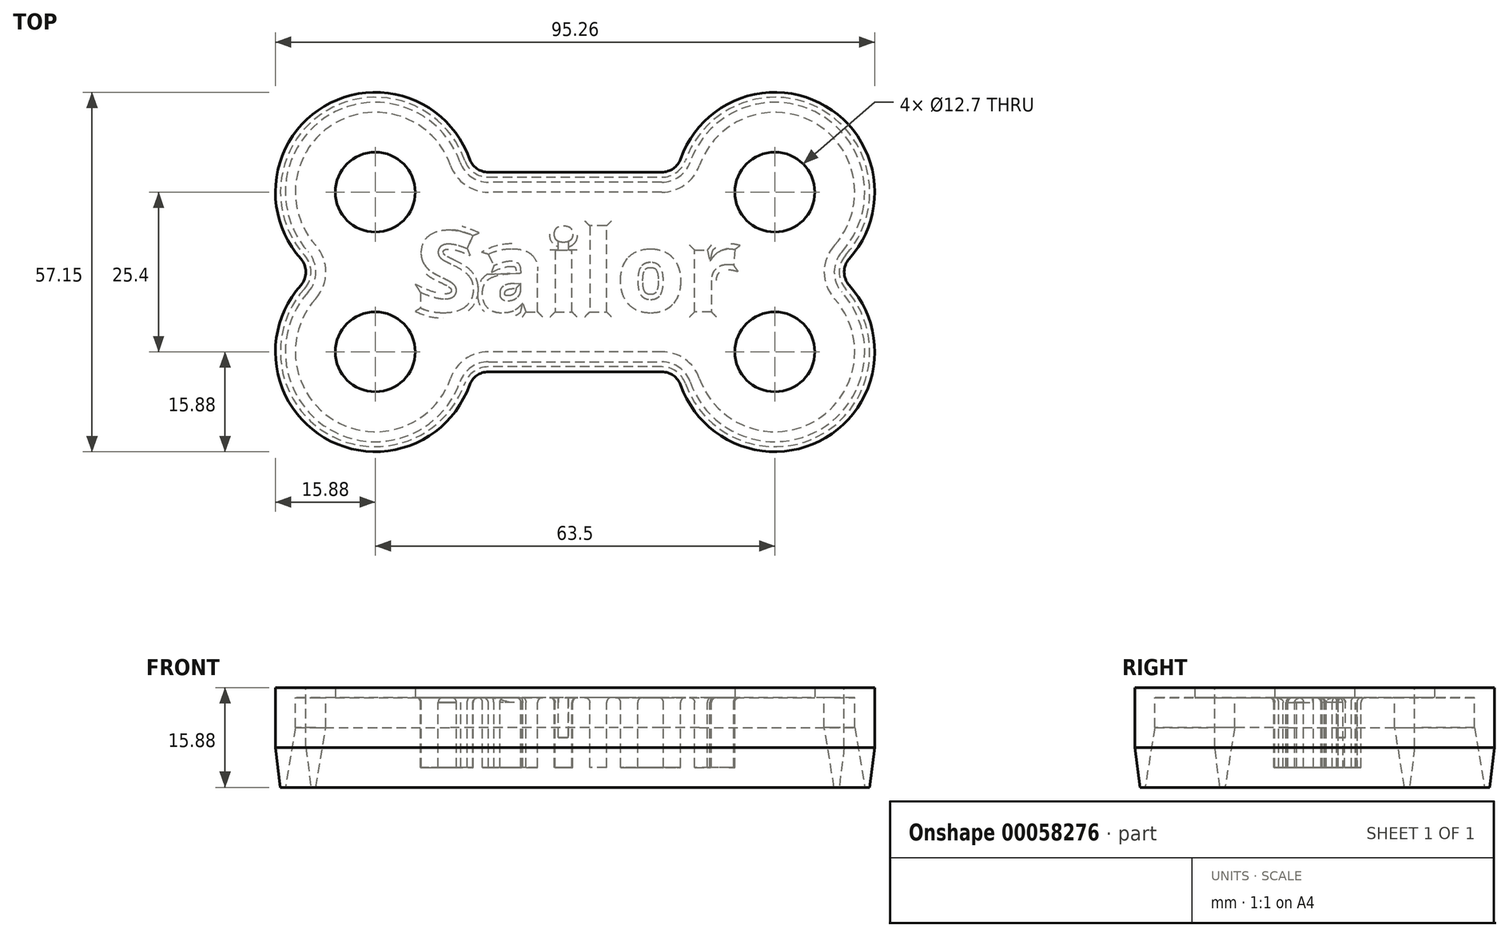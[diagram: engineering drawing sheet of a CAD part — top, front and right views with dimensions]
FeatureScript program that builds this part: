
annotation { "Feature Type Name" : "Feature", "Feature Type Description" : "" }
export const myFeature = defineFeature(function(context is Context, id is Id, definition is map)
    precondition{}
    {
        {
            var Q0;
            Q0=qCreatedBy(makeId("Top.planeOp"),FACE);
            var sketch = newSketch(context, id + "F0", { "sketchPlane" : qUnion([Q0])});
            skText(sketch, "E0", { "text": "Sailor", "fontName": "OpenSans-Bold.ttf"});
            const initialGuessF0  = {"E0": [0, 0, 1, 0, 0.01298]};
            skSetInitialGuess(sketch, initialGuessF0);
            skSolve(sketch);
        }
        {
            var Q0;
            Q0 = qSketchRegion(id + "F0", true);
            extrude(context, id + "F1", {"entities" : qUnion([Q0]), "oppositeDirection" : true, "depth" : 12.7 * mm});
        }
        {
            var Q0;
            Q0=qCreatedBy(makeId("Top.planeOp"),FACE);
            var sketch = newSketch(context, id + "F2", { "sketchPlane" : qUnion([Q0])});
            skLineSegment(sketch, "E1.bottom", {"start": v(11.61, 19.05) * mm, "end": v(39.19, 19.05) * mm});
            skLineSegment(sketch, "E1.top", {"start": v(11.61, -6.35) * mm, "end": v(39.19, -6.35) * mm});
            skArc(sketch, "E2", {"start": v(5.62, 23.28) * mm, "mid": v(-12.82, 29.98) * mm, "end": v(-15.82, 10.58) * mm});
            skArc(sketch, "E3", {"start": v(-15.82, 2.12) * mm, "mid": v(-12.82, -17.28) * mm, "end": v(5.62, -10.58) * mm});
            skArc(sketch, "E4", {"start": v(66.62, 10.58) * mm, "mid": v(63.62, 29.98) * mm, "end": v(45.18, 23.28) * mm});
            skArc(sketch, "E5", {"start": v(45.18, -10.58) * mm, "mid": v(63.62, -17.28) * mm, "end": v(66.62, 2.12) * mm});
            skPoint(sketch, "E6.visualSharp", {"position": v(-6.35, 6.35) * mm});
            skArc(sketch, "E6.filletArc", {"start": v(-15.82, 2.12) * mm, "mid": v(-14.2, 6.35) * mm, "end": v(-15.82, 10.58) * mm});
            skPoint(sketch, "E7.visualSharp", {"position": v(57.15, 6.35) * mm});
            skArc(sketch, "E7.filletArc", {"start": v(66.62, 10.58) * mm, "mid": v(65, 6.35) * mm, "end": v(66.62, 2.12) * mm});
            skPoint(sketch, "E8.visualSharp", {"position": v(44.45, 19.05) * mm});
            skArc(sketch, "E8.filletArc", {"start": v(39.19, 19.05) * mm, "mid": v(42.86, 20.22) * mm, "end": v(45.18, 23.28) * mm});
            skPoint(sketch, "E9.visualSharp", {"position": v(6.35, 19.05) * mm});
            skArc(sketch, "E9.filletArc", {"start": v(5.62, 23.28) * mm, "mid": v(7.94, 20.22) * mm, "end": v(11.61, 19.05) * mm});
            skPoint(sketch, "E10.visualSharp", {"position": v(6.35, -6.35) * mm});
            skArc(sketch, "E10.filletArc", {"start": v(11.61, -6.35) * mm, "mid": v(7.94, -7.52) * mm, "end": v(5.62, -10.58) * mm});
            skPoint(sketch, "E11.visualSharp", {"position": v(44.45, -6.35) * mm});
            skArc(sketch, "E11.filletArc", {"start": v(45.18, -10.58) * mm, "mid": v(42.86, -7.52) * mm, "end": v(39.19, -6.35) * mm});
            skArc(sketch, "E12.0", {"start": v(8.62, 24.34) * mm, "mid": v(9.78, 22.8) * mm, "end": v(11.61, 22.23) * mm});
            skArc(sketch, "E12.1", {"start": v(42.18, -11.64) * mm, "mid": v(65.24, -20) * mm, "end": v(68.98, 4.23) * mm});
            skArc(sketch, "E12.2", {"start": v(68.98, 8.47) * mm, "mid": v(68.17, 6.35) * mm, "end": v(68.98, 4.23) * mm});
            skArc(sketch, "E12.3", {"start": v(68.98, 8.47) * mm, "mid": v(65.24, 32.7) * mm, "end": v(42.18, 24.34) * mm});
            skArc(sketch, "E12.4", {"start": v(39.19, 22.23) * mm, "mid": v(41.02, 22.8) * mm, "end": v(42.18, 24.34) * mm});
            skArc(sketch, "E12.5", {"start": v(42.18, -11.64) * mm, "mid": v(41.02, -10.1) * mm, "end": v(39.19, -9.52) * mm});
            skLineSegment(sketch, "E12.6", {"start": v(11.61, 22.22) * mm, "end": v(39.19, 22.23) * mm});
            skLineSegment(sketch, "E12.7", {"start": v(11.61, -9.53) * mm, "end": v(39.19, -9.52) * mm});
            skArc(sketch, "E12.8", {"start": v(11.61, -9.53) * mm, "mid": v(9.78, -10.1) * mm, "end": v(8.62, -11.64) * mm});
            skArc(sketch, "E12.9", {"start": v(-18.18, 4.23) * mm, "mid": v(-14.44, -20) * mm, "end": v(8.62, -11.64) * mm});
            skArc(sketch, "E12.10", {"start": v(-18.18, 4.23) * mm, "mid": v(-17.37, 6.35) * mm, "end": v(-18.18, 8.47) * mm});
            skArc(sketch, "E12.11", {"start": v(8.62, 24.34) * mm, "mid": v(-14.44, 32.7) * mm, "end": v(-18.18, 8.47) * mm});
            skSolve(sketch);
        }
        {
            var Q0;
            Q0 = qSketchRegion(id + "F2", true);
            extrude(context, id + "F3", {"entities" : qUnion([Q0]), "oppositeDirection" : true, "depth" : 15.88 * mm});
        }
        {
            var Q0;
            Q0=qCreatedBy(makeId("Top.planeOp"),FACE);
            var sketch = newSketch(context, id + "F4", { "sketchPlane" : qUnion([Q0])});
            skArc(sketch, "E13.0", {"start": v(-18.18, 8.47) * mm, "mid": v(-14.44, 32.7) * mm, "end": v(8.62, 24.34) * mm});
            skArc(sketch, "E14.0", {"start": v(8.62, 24.34) * mm, "mid": v(9.78, 22.8) * mm, "end": v(11.61, 22.23) * mm});
            skLineSegment(sketch, "E15.0", {"start": v(11.61, 22.22) * mm, "end": v(39.19, 22.23) * mm});
            skArc(sketch, "E16.0", {"start": v(39.19, 22.23) * mm, "mid": v(41.02, 22.8) * mm, "end": v(42.18, 24.34) * mm});
            skArc(sketch, "E17.0", {"start": v(42.18, 24.34) * mm, "mid": v(65.24, 32.7) * mm, "end": v(68.98, 8.47) * mm});
            skArc(sketch, "E18.0", {"start": v(68.98, 8.47) * mm, "mid": v(68.17, 6.35) * mm, "end": v(68.98, 4.23) * mm});
            skArc(sketch, "E19.0", {"start": v(68.98, 4.23) * mm, "mid": v(65.24, -20) * mm, "end": v(42.18, -11.64) * mm});
            skArc(sketch, "E20.0", {"start": v(42.18, -11.64) * mm, "mid": v(41.02, -10.1) * mm, "end": v(39.19, -9.52) * mm});
            skLineSegment(sketch, "E21.0", {"start": v(39.19, -9.52) * mm, "end": v(11.61, -9.53) * mm});
            skArc(sketch, "E22.0", {"start": v(11.61, -9.53) * mm, "mid": v(9.78, -10.1) * mm, "end": v(8.62, -11.64) * mm});
            skArc(sketch, "E23.0", {"start": v(8.62, -11.64) * mm, "mid": v(-14.44, -20) * mm, "end": v(-18.18, 4.23) * mm});
            skArc(sketch, "E24.0", {"start": v(-18.18, 4.23) * mm, "mid": v(-17.37, 6.35) * mm, "end": v(-18.18, 8.47) * mm});
            skSolve(sketch);
        }
        {
            var Q0;
            Q0 = qSketchRegion(id + "F4", true);
            extrude(context, id + "F5", {"entities" : qUnion([Q0]), "operationType" : NewBodyOperationType.ADD, "oppositeDirection" : true, "depth" : 1.59 * mm});
        }
        {
            var Q0;
            Q0=makeQuery(id+"F5.boolean.opBoolean","SPLIT",FACE,{"disambiguationData":[TD([makeQuery(id+"F1.opExtrude","SWEPT_FACE",FACE,{"disambiguationData":[OSD([sQuery(id+"F0.wireOp",EDGE,"E0.sketch_text.stroke-0")])]})])],"derivedFrom":makeQuery(id+"F5.opExtrude","CAP_FACE",FACE,{"disambiguationData":[OSD([sQuery(id+"F4.wireOp",EDGE,"E13.0"),sQuery(id+"F4.wireOp",EDGE,"E14.0"),sQuery(id+"F4.wireOp",EDGE,"E15.0"),sQuery(id+"F4.wireOp",EDGE,"E16.0"),sQuery(id+"F4.wireOp",EDGE,"E17.0"),sQuery(id+"F4.wireOp",EDGE,"E18.0"),sQuery(id+"F4.wireOp",EDGE,"E19.0"),sQuery(id+"F4.wireOp",EDGE,"E20.0"),sQuery(id+"F4.wireOp",EDGE,"E21.0"),sQuery(id+"F4.wireOp",EDGE,"E22.0"),sQuery(id+"F4.wireOp",EDGE,"E23.0"),sQuery(id+"F4.wireOp",EDGE,"E24.0")])],"isStart":false})});
            var sketch = newSketch(context, id + "F6", { "sketchPlane" : qUnion([Q0])});
            skLineSegment(sketch, "E25", {"start": v(22.73, -8.79) * mm, "end": v(22.73, -11.84) * mm});
            skLineSegment(sketch, "E26", {"start": v(22.73, -11.84) * mm, "end": v(24.32, -11.84) * mm});
            skLineSegment(sketch, "E27", {"start": v(24.32, -11.84) * mm, "end": v(24.32, -8.79) * mm});
            skLineSegment(sketch, "E28", {"start": v(24.32, -8.79) * mm, "end": v(22.73, -8.79) * mm});
            skSolve(sketch);
        }
        {
            var Q0;
            Q0 = qSketchRegion(id + "F6", true);
            extrude(context, id + "F7", {"entities" : qUnion([Q0]), "operationType" : NewBodyOperationType.ADD, "depth" : 6.35 * mm});
        }
        {
            var Q0;
            Q0=makeQuery(id+"F5.boolean.opBoolean","INTERSECT",EDGE,{"derivedFrom":[makeQuery(id+"F1.opExtrude","SWEPT_FACE",FACE,{"disambiguationData":[OSD([sQuery(id+"F0.wireOp",EDGE,"E0.sketch_text.stroke-14")])]}),makeQuery(id+"F5.opExtrude","CAP_FACE",FACE,{"disambiguationData":[OSD([sQuery(id+"F4.wireOp",EDGE,"E13.0"),sQuery(id+"F4.wireOp",EDGE,"E14.0"),sQuery(id+"F4.wireOp",EDGE,"E15.0"),sQuery(id+"F4.wireOp",EDGE,"E16.0"),sQuery(id+"F4.wireOp",EDGE,"E17.0"),sQuery(id+"F4.wireOp",EDGE,"E18.0"),sQuery(id+"F4.wireOp",EDGE,"E19.0"),sQuery(id+"F4.wireOp",EDGE,"E20.0"),sQuery(id+"F4.wireOp",EDGE,"E21.0"),sQuery(id+"F4.wireOp",EDGE,"E22.0"),sQuery(id+"F4.wireOp",EDGE,"E23.0"),sQuery(id+"F4.wireOp",EDGE,"E24.0")])],"isStart":false})]});
            var Q1;
            Q1=makeQuery(id+"F5.boolean.opBoolean","INTERSECT",EDGE,{"derivedFrom":[makeQuery(id+"F1.opExtrude","SWEPT_FACE",FACE,{"disambiguationData":[OSD([sQuery(id+"F0.wireOp",EDGE,"E0.sketch_text.stroke-7")])]}),makeQuery(id+"F5.opExtrude","CAP_FACE",FACE,{"disambiguationData":[OSD([sQuery(id+"F4.wireOp",EDGE,"E13.0"),sQuery(id+"F4.wireOp",EDGE,"E14.0"),sQuery(id+"F4.wireOp",EDGE,"E15.0"),sQuery(id+"F4.wireOp",EDGE,"E16.0"),sQuery(id+"F4.wireOp",EDGE,"E17.0"),sQuery(id+"F4.wireOp",EDGE,"E18.0"),sQuery(id+"F4.wireOp",EDGE,"E19.0"),sQuery(id+"F4.wireOp",EDGE,"E20.0"),sQuery(id+"F4.wireOp",EDGE,"E21.0"),sQuery(id+"F4.wireOp",EDGE,"E22.0"),sQuery(id+"F4.wireOp",EDGE,"E23.0"),sQuery(id+"F4.wireOp",EDGE,"E24.0")])],"isStart":false})]});
            var Q2;
            Q2=makeQuery(id+"F5.boolean.opBoolean","INTERSECT",EDGE,{"derivedFrom":[makeQuery(id+"F1.opExtrude","SWEPT_FACE",FACE,{"disambiguationData":[OSD([sQuery(id+"F0.wireOp",EDGE,"E0.sketch_text.stroke-3")])]}),makeQuery(id+"F5.opExtrude","CAP_FACE",FACE,{"disambiguationData":[OSD([sQuery(id+"F4.wireOp",EDGE,"E13.0"),sQuery(id+"F4.wireOp",EDGE,"E14.0"),sQuery(id+"F4.wireOp",EDGE,"E15.0"),sQuery(id+"F4.wireOp",EDGE,"E16.0"),sQuery(id+"F4.wireOp",EDGE,"E17.0"),sQuery(id+"F4.wireOp",EDGE,"E18.0"),sQuery(id+"F4.wireOp",EDGE,"E19.0"),sQuery(id+"F4.wireOp",EDGE,"E20.0"),sQuery(id+"F4.wireOp",EDGE,"E21.0"),sQuery(id+"F4.wireOp",EDGE,"E22.0"),sQuery(id+"F4.wireOp",EDGE,"E23.0"),sQuery(id+"F4.wireOp",EDGE,"E24.0")])],"isStart":false})]});
            var Q3;
            Q3=makeQuery(id+"F5.boolean.opBoolean","INTERSECT",EDGE,{"derivedFrom":[makeQuery(id+"F1.opExtrude","SWEPT_FACE",FACE,{"disambiguationData":[OSD([sQuery(id+"F0.wireOp",EDGE,"E0.sketch_text.stroke-1")])]}),makeQuery(id+"F5.opExtrude","CAP_FACE",FACE,{"disambiguationData":[OSD([sQuery(id+"F4.wireOp",EDGE,"E13.0"),sQuery(id+"F4.wireOp",EDGE,"E14.0"),sQuery(id+"F4.wireOp",EDGE,"E15.0"),sQuery(id+"F4.wireOp",EDGE,"E16.0"),sQuery(id+"F4.wireOp",EDGE,"E17.0"),sQuery(id+"F4.wireOp",EDGE,"E18.0"),sQuery(id+"F4.wireOp",EDGE,"E19.0"),sQuery(id+"F4.wireOp",EDGE,"E20.0"),sQuery(id+"F4.wireOp",EDGE,"E21.0"),sQuery(id+"F4.wireOp",EDGE,"E22.0"),sQuery(id+"F4.wireOp",EDGE,"E23.0"),sQuery(id+"F4.wireOp",EDGE,"E24.0")])],"isStart":false})]});
            var Q4;
            Q4=makeQuery(id+"F5.boolean.opBoolean","INTERSECT",EDGE,{"derivedFrom":[makeQuery(id+"F1.opExtrude","SWEPT_FACE",FACE,{"disambiguationData":[OSD([sQuery(id+"F0.wireOp",EDGE,"E0.sketch_text.stroke-20")])]}),makeQuery(id+"F5.opExtrude","CAP_FACE",FACE,{"disambiguationData":[OSD([sQuery(id+"F4.wireOp",EDGE,"E13.0"),sQuery(id+"F4.wireOp",EDGE,"E14.0"),sQuery(id+"F4.wireOp",EDGE,"E15.0"),sQuery(id+"F4.wireOp",EDGE,"E16.0"),sQuery(id+"F4.wireOp",EDGE,"E17.0"),sQuery(id+"F4.wireOp",EDGE,"E18.0"),sQuery(id+"F4.wireOp",EDGE,"E19.0"),sQuery(id+"F4.wireOp",EDGE,"E20.0"),sQuery(id+"F4.wireOp",EDGE,"E21.0"),sQuery(id+"F4.wireOp",EDGE,"E22.0"),sQuery(id+"F4.wireOp",EDGE,"E23.0"),sQuery(id+"F4.wireOp",EDGE,"E24.0")])],"isStart":false})]});
            var Q5;
            Q5=makeQuery(id+"F5.boolean.opBoolean","INTERSECT",EDGE,{"derivedFrom":[makeQuery(id+"F1.opExtrude","SWEPT_FACE",FACE,{"disambiguationData":[OSD([sQuery(id+"F0.wireOp",EDGE,"E0.sketch_text.stroke-18")])]}),makeQuery(id+"F5.opExtrude","CAP_FACE",FACE,{"disambiguationData":[OSD([sQuery(id+"F4.wireOp",EDGE,"E13.0"),sQuery(id+"F4.wireOp",EDGE,"E14.0"),sQuery(id+"F4.wireOp",EDGE,"E15.0"),sQuery(id+"F4.wireOp",EDGE,"E16.0"),sQuery(id+"F4.wireOp",EDGE,"E17.0"),sQuery(id+"F4.wireOp",EDGE,"E18.0"),sQuery(id+"F4.wireOp",EDGE,"E19.0"),sQuery(id+"F4.wireOp",EDGE,"E20.0"),sQuery(id+"F4.wireOp",EDGE,"E21.0"),sQuery(id+"F4.wireOp",EDGE,"E22.0"),sQuery(id+"F4.wireOp",EDGE,"E23.0"),sQuery(id+"F4.wireOp",EDGE,"E24.0")])],"isStart":false})]});
            var Q6;
            Q6=makeQuery(id+"F5.boolean.opBoolean","INTERSECT",EDGE,{"derivedFrom":[makeQuery(id+"F1.opExtrude","SWEPT_FACE",FACE,{"disambiguationData":[OSD([sQuery(id+"F0.wireOp",EDGE,"E0.sketch_text.stroke-32")])]}),makeQuery(id+"F5.opExtrude","CAP_FACE",FACE,{"disambiguationData":[OSD([sQuery(id+"F4.wireOp",EDGE,"E13.0"),sQuery(id+"F4.wireOp",EDGE,"E14.0"),sQuery(id+"F4.wireOp",EDGE,"E15.0"),sQuery(id+"F4.wireOp",EDGE,"E16.0"),sQuery(id+"F4.wireOp",EDGE,"E17.0"),sQuery(id+"F4.wireOp",EDGE,"E18.0"),sQuery(id+"F4.wireOp",EDGE,"E19.0"),sQuery(id+"F4.wireOp",EDGE,"E20.0"),sQuery(id+"F4.wireOp",EDGE,"E21.0"),sQuery(id+"F4.wireOp",EDGE,"E22.0"),sQuery(id+"F4.wireOp",EDGE,"E23.0"),sQuery(id+"F4.wireOp",EDGE,"E24.0")])],"isStart":false})]});
            var Q7;
            Q7=makeQuery(id+"F5.boolean.opBoolean","INTERSECT",EDGE,{"derivedFrom":[makeQuery(id+"F1.opExtrude","SWEPT_FACE",FACE,{"disambiguationData":[OSD([sQuery(id+"F0.wireOp",EDGE,"E0.sketch_text.stroke-28")])]}),makeQuery(id+"F5.opExtrude","CAP_FACE",FACE,{"disambiguationData":[OSD([sQuery(id+"F4.wireOp",EDGE,"E13.0"),sQuery(id+"F4.wireOp",EDGE,"E14.0"),sQuery(id+"F4.wireOp",EDGE,"E15.0"),sQuery(id+"F4.wireOp",EDGE,"E16.0"),sQuery(id+"F4.wireOp",EDGE,"E17.0"),sQuery(id+"F4.wireOp",EDGE,"E18.0"),sQuery(id+"F4.wireOp",EDGE,"E19.0"),sQuery(id+"F4.wireOp",EDGE,"E20.0"),sQuery(id+"F4.wireOp",EDGE,"E21.0"),sQuery(id+"F4.wireOp",EDGE,"E22.0"),sQuery(id+"F4.wireOp",EDGE,"E23.0"),sQuery(id+"F4.wireOp",EDGE,"E24.0")])],"isStart":false})]});
            var Q8;
            Q8=makeQuery(id+"F5.boolean.opBoolean","INTERSECT",EDGE,{"derivedFrom":[makeQuery(id+"F1.opExtrude","SWEPT_FACE",FACE,{"disambiguationData":[OSD([sQuery(id+"F0.wireOp",EDGE,"E0.sketch_text.stroke-45")])]}),makeQuery(id+"F5.opExtrude","CAP_FACE",FACE,{"disambiguationData":[OSD([sQuery(id+"F4.wireOp",EDGE,"E13.0"),sQuery(id+"F4.wireOp",EDGE,"E14.0"),sQuery(id+"F4.wireOp",EDGE,"E15.0"),sQuery(id+"F4.wireOp",EDGE,"E16.0"),sQuery(id+"F4.wireOp",EDGE,"E17.0"),sQuery(id+"F4.wireOp",EDGE,"E18.0"),sQuery(id+"F4.wireOp",EDGE,"E19.0"),sQuery(id+"F4.wireOp",EDGE,"E20.0"),sQuery(id+"F4.wireOp",EDGE,"E21.0"),sQuery(id+"F4.wireOp",EDGE,"E22.0"),sQuery(id+"F4.wireOp",EDGE,"E23.0"),sQuery(id+"F4.wireOp",EDGE,"E24.0")])],"isStart":false})]});
            var Q9;
            Q9=makeQuery(id+"F5.boolean.opBoolean","INTERSECT",EDGE,{"derivedFrom":[makeQuery(id+"F1.opExtrude","SWEPT_FACE",FACE,{"disambiguationData":[OSD([sQuery(id+"F0.wireOp",EDGE,"E0.sketch_text.stroke-44")])]}),makeQuery(id+"F5.opExtrude","CAP_FACE",FACE,{"disambiguationData":[OSD([sQuery(id+"F4.wireOp",EDGE,"E13.0"),sQuery(id+"F4.wireOp",EDGE,"E14.0"),sQuery(id+"F4.wireOp",EDGE,"E15.0"),sQuery(id+"F4.wireOp",EDGE,"E16.0"),sQuery(id+"F4.wireOp",EDGE,"E17.0"),sQuery(id+"F4.wireOp",EDGE,"E18.0"),sQuery(id+"F4.wireOp",EDGE,"E19.0"),sQuery(id+"F4.wireOp",EDGE,"E20.0"),sQuery(id+"F4.wireOp",EDGE,"E21.0"),sQuery(id+"F4.wireOp",EDGE,"E22.0"),sQuery(id+"F4.wireOp",EDGE,"E23.0"),sQuery(id+"F4.wireOp",EDGE,"E24.0")])],"isStart":false})]});
            var Q10;
            Q10=makeQuery(id+"F5.boolean.opBoolean","INTERSECT",EDGE,{"derivedFrom":[makeQuery(id+"F1.opExtrude","SWEPT_FACE",FACE,{"disambiguationData":[OSD([sQuery(id+"F0.wireOp",EDGE,"E0.sketch_text.stroke-40")])]}),makeQuery(id+"F5.opExtrude","CAP_FACE",FACE,{"disambiguationData":[OSD([sQuery(id+"F4.wireOp",EDGE,"E13.0"),sQuery(id+"F4.wireOp",EDGE,"E14.0"),sQuery(id+"F4.wireOp",EDGE,"E15.0"),sQuery(id+"F4.wireOp",EDGE,"E16.0"),sQuery(id+"F4.wireOp",EDGE,"E17.0"),sQuery(id+"F4.wireOp",EDGE,"E18.0"),sQuery(id+"F4.wireOp",EDGE,"E19.0"),sQuery(id+"F4.wireOp",EDGE,"E20.0"),sQuery(id+"F4.wireOp",EDGE,"E21.0"),sQuery(id+"F4.wireOp",EDGE,"E22.0"),sQuery(id+"F4.wireOp",EDGE,"E23.0"),sQuery(id+"F4.wireOp",EDGE,"E24.0")])],"isStart":false})]});
            var Q11;
            Q11=makeQuery(id+"F5.boolean.opBoolean","INTERSECT",EDGE,{"derivedFrom":[makeQuery(id+"F1.opExtrude","SWEPT_FACE",FACE,{"disambiguationData":[OSD([sQuery(id+"F0.wireOp",EDGE,"E0.sketch_text.stroke-39")])]}),makeQuery(id+"F5.opExtrude","CAP_FACE",FACE,{"disambiguationData":[OSD([sQuery(id+"F4.wireOp",EDGE,"E13.0"),sQuery(id+"F4.wireOp",EDGE,"E14.0"),sQuery(id+"F4.wireOp",EDGE,"E15.0"),sQuery(id+"F4.wireOp",EDGE,"E16.0"),sQuery(id+"F4.wireOp",EDGE,"E17.0"),sQuery(id+"F4.wireOp",EDGE,"E18.0"),sQuery(id+"F4.wireOp",EDGE,"E19.0"),sQuery(id+"F4.wireOp",EDGE,"E20.0"),sQuery(id+"F4.wireOp",EDGE,"E21.0"),sQuery(id+"F4.wireOp",EDGE,"E22.0"),sQuery(id+"F4.wireOp",EDGE,"E23.0"),sQuery(id+"F4.wireOp",EDGE,"E24.0")])],"isStart":false})]});
            var Q12;
            Q12=makeQuery(id+"F5.boolean.opBoolean","INTERSECT",EDGE,{"derivedFrom":[makeQuery(id+"F1.opExtrude","SWEPT_FACE",FACE,{"disambiguationData":[OSD([sQuery(id+"F0.wireOp",EDGE,"E0.sketch_text.stroke-52")])]}),makeQuery(id+"F5.opExtrude","CAP_FACE",FACE,{"disambiguationData":[OSD([sQuery(id+"F4.wireOp",EDGE,"E13.0"),sQuery(id+"F4.wireOp",EDGE,"E14.0"),sQuery(id+"F4.wireOp",EDGE,"E15.0"),sQuery(id+"F4.wireOp",EDGE,"E16.0"),sQuery(id+"F4.wireOp",EDGE,"E17.0"),sQuery(id+"F4.wireOp",EDGE,"E18.0"),sQuery(id+"F4.wireOp",EDGE,"E19.0"),sQuery(id+"F4.wireOp",EDGE,"E20.0"),sQuery(id+"F4.wireOp",EDGE,"E21.0"),sQuery(id+"F4.wireOp",EDGE,"E22.0"),sQuery(id+"F4.wireOp",EDGE,"E23.0"),sQuery(id+"F4.wireOp",EDGE,"E24.0")])],"isStart":false})]});
            var Q13;
            Q13=makeQuery(id+"F5.boolean.opBoolean","INTERSECT",EDGE,{"derivedFrom":[makeQuery(id+"F1.opExtrude","SWEPT_FACE",FACE,{"disambiguationData":[OSD([sQuery(id+"F0.wireOp",EDGE,"E0.sketch_text.stroke-59")])]}),makeQuery(id+"F5.opExtrude","CAP_FACE",FACE,{"disambiguationData":[OSD([sQuery(id+"F4.wireOp",EDGE,"E13.0"),sQuery(id+"F4.wireOp",EDGE,"E14.0"),sQuery(id+"F4.wireOp",EDGE,"E15.0"),sQuery(id+"F4.wireOp",EDGE,"E16.0"),sQuery(id+"F4.wireOp",EDGE,"E17.0"),sQuery(id+"F4.wireOp",EDGE,"E18.0"),sQuery(id+"F4.wireOp",EDGE,"E19.0"),sQuery(id+"F4.wireOp",EDGE,"E20.0"),sQuery(id+"F4.wireOp",EDGE,"E21.0"),sQuery(id+"F4.wireOp",EDGE,"E22.0"),sQuery(id+"F4.wireOp",EDGE,"E23.0"),sQuery(id+"F4.wireOp",EDGE,"E24.0")])],"isStart":false})]});
            var Q14;
            Q14=makeQuery(id+"F5.boolean.opBoolean","INTERSECT",EDGE,{"derivedFrom":[makeQuery(id+"F1.opExtrude","SWEPT_FACE",FACE,{"disambiguationData":[OSD([sQuery(id+"F0.wireOp",EDGE,"E0.sketch_text.stroke-58")])]}),makeQuery(id+"F5.opExtrude","CAP_FACE",FACE,{"disambiguationData":[OSD([sQuery(id+"F4.wireOp",EDGE,"E13.0"),sQuery(id+"F4.wireOp",EDGE,"E14.0"),sQuery(id+"F4.wireOp",EDGE,"E15.0"),sQuery(id+"F4.wireOp",EDGE,"E16.0"),sQuery(id+"F4.wireOp",EDGE,"E17.0"),sQuery(id+"F4.wireOp",EDGE,"E18.0"),sQuery(id+"F4.wireOp",EDGE,"E19.0"),sQuery(id+"F4.wireOp",EDGE,"E20.0"),sQuery(id+"F4.wireOp",EDGE,"E21.0"),sQuery(id+"F4.wireOp",EDGE,"E22.0"),sQuery(id+"F4.wireOp",EDGE,"E23.0"),sQuery(id+"F4.wireOp",EDGE,"E24.0")])],"isStart":false})]});
            var Q15;
            Q15=makeQuery(id+"F5.boolean.opBoolean","INTERSECT",EDGE,{"derivedFrom":[makeQuery(id+"F1.opExtrude","SWEPT_FACE",FACE,{"disambiguationData":[OSD([sQuery(id+"F0.wireOp",EDGE,"E0.sketch_text.stroke-61")])]}),makeQuery(id+"F5.opExtrude","CAP_FACE",FACE,{"disambiguationData":[OSD([sQuery(id+"F4.wireOp",EDGE,"E13.0"),sQuery(id+"F4.wireOp",EDGE,"E14.0"),sQuery(id+"F4.wireOp",EDGE,"E15.0"),sQuery(id+"F4.wireOp",EDGE,"E16.0"),sQuery(id+"F4.wireOp",EDGE,"E17.0"),sQuery(id+"F4.wireOp",EDGE,"E18.0"),sQuery(id+"F4.wireOp",EDGE,"E19.0"),sQuery(id+"F4.wireOp",EDGE,"E20.0"),sQuery(id+"F4.wireOp",EDGE,"E21.0"),sQuery(id+"F4.wireOp",EDGE,"E22.0"),sQuery(id+"F4.wireOp",EDGE,"E23.0"),sQuery(id+"F4.wireOp",EDGE,"E24.0")])],"isStart":false})]});
            var Q16;
            Q16=makeQuery(id+"F5.boolean.opBoolean","INTERSECT",EDGE,{"derivedFrom":[makeQuery(id+"F1.opExtrude","SWEPT_FACE",FACE,{"disambiguationData":[OSD([sQuery(id+"F0.wireOp",EDGE,"E0.sketch_text.stroke-62")])]}),makeQuery(id+"F5.opExtrude","CAP_FACE",FACE,{"disambiguationData":[OSD([sQuery(id+"F4.wireOp",EDGE,"E13.0"),sQuery(id+"F4.wireOp",EDGE,"E14.0"),sQuery(id+"F4.wireOp",EDGE,"E15.0"),sQuery(id+"F4.wireOp",EDGE,"E16.0"),sQuery(id+"F4.wireOp",EDGE,"E17.0"),sQuery(id+"F4.wireOp",EDGE,"E18.0"),sQuery(id+"F4.wireOp",EDGE,"E19.0"),sQuery(id+"F4.wireOp",EDGE,"E20.0"),sQuery(id+"F4.wireOp",EDGE,"E21.0"),sQuery(id+"F4.wireOp",EDGE,"E22.0"),sQuery(id+"F4.wireOp",EDGE,"E23.0"),sQuery(id+"F4.wireOp",EDGE,"E24.0")])],"isStart":false})]});
            var Q17;
            Q17=makeQuery(id+"F5.boolean.opBoolean","INTERSECT",EDGE,{"derivedFrom":[makeQuery(id+"F1.opExtrude","SWEPT_FACE",FACE,{"disambiguationData":[OSD([sQuery(id+"F0.wireOp",EDGE,"E0.sketch_text.stroke-65")])]}),makeQuery(id+"F5.opExtrude","CAP_FACE",FACE,{"disambiguationData":[OSD([sQuery(id+"F4.wireOp",EDGE,"E13.0"),sQuery(id+"F4.wireOp",EDGE,"E14.0"),sQuery(id+"F4.wireOp",EDGE,"E15.0"),sQuery(id+"F4.wireOp",EDGE,"E16.0"),sQuery(id+"F4.wireOp",EDGE,"E17.0"),sQuery(id+"F4.wireOp",EDGE,"E18.0"),sQuery(id+"F4.wireOp",EDGE,"E19.0"),sQuery(id+"F4.wireOp",EDGE,"E20.0"),sQuery(id+"F4.wireOp",EDGE,"E21.0"),sQuery(id+"F4.wireOp",EDGE,"E22.0"),sQuery(id+"F4.wireOp",EDGE,"E23.0"),sQuery(id+"F4.wireOp",EDGE,"E24.0")])],"isStart":false})]});
            var Q18;
            Q18=makeQuery(id+"F5.boolean.opBoolean","INTERSECT",EDGE,{"derivedFrom":[makeQuery(id+"F1.opExtrude","SWEPT_FACE",FACE,{"disambiguationData":[OSD([sQuery(id+"F0.wireOp",EDGE,"E0.sketch_text.stroke-55")])]}),makeQuery(id+"F5.opExtrude","CAP_FACE",FACE,{"disambiguationData":[OSD([sQuery(id+"F4.wireOp",EDGE,"E13.0"),sQuery(id+"F4.wireOp",EDGE,"E14.0"),sQuery(id+"F4.wireOp",EDGE,"E15.0"),sQuery(id+"F4.wireOp",EDGE,"E16.0"),sQuery(id+"F4.wireOp",EDGE,"E17.0"),sQuery(id+"F4.wireOp",EDGE,"E18.0"),sQuery(id+"F4.wireOp",EDGE,"E19.0"),sQuery(id+"F4.wireOp",EDGE,"E20.0"),sQuery(id+"F4.wireOp",EDGE,"E21.0"),sQuery(id+"F4.wireOp",EDGE,"E22.0"),sQuery(id+"F4.wireOp",EDGE,"E23.0"),sQuery(id+"F4.wireOp",EDGE,"E24.0")])],"isStart":false})]});
            var Q19;
            Q19=makeQuery(id+"F5.boolean.opBoolean","INTERSECT",EDGE,{"derivedFrom":[makeQuery(id+"F1.opExtrude","SWEPT_FACE",FACE,{"disambiguationData":[OSD([sQuery(id+"F0.wireOp",EDGE,"E0.sketch_text.stroke-63")])]}),makeQuery(id+"F5.opExtrude","CAP_FACE",FACE,{"disambiguationData":[OSD([sQuery(id+"F4.wireOp",EDGE,"E13.0"),sQuery(id+"F4.wireOp",EDGE,"E14.0"),sQuery(id+"F4.wireOp",EDGE,"E15.0"),sQuery(id+"F4.wireOp",EDGE,"E16.0"),sQuery(id+"F4.wireOp",EDGE,"E17.0"),sQuery(id+"F4.wireOp",EDGE,"E18.0"),sQuery(id+"F4.wireOp",EDGE,"E19.0"),sQuery(id+"F4.wireOp",EDGE,"E20.0"),sQuery(id+"F4.wireOp",EDGE,"E21.0"),sQuery(id+"F4.wireOp",EDGE,"E22.0"),sQuery(id+"F4.wireOp",EDGE,"E23.0"),sQuery(id+"F4.wireOp",EDGE,"E24.0")])],"isStart":false})]});
            var Q20;
            Q20=makeQuery(id+"F5.boolean.opBoolean","INTERSECT",EDGE,{"derivedFrom":[makeQuery(id+"F1.opExtrude","SWEPT_FACE",FACE,{"disambiguationData":[OSD([sQuery(id+"F0.wireOp",EDGE,"E0.sketch_text.stroke-64")])]}),makeQuery(id+"F5.opExtrude","CAP_FACE",FACE,{"disambiguationData":[OSD([sQuery(id+"F4.wireOp",EDGE,"E13.0"),sQuery(id+"F4.wireOp",EDGE,"E14.0"),sQuery(id+"F4.wireOp",EDGE,"E15.0"),sQuery(id+"F4.wireOp",EDGE,"E16.0"),sQuery(id+"F4.wireOp",EDGE,"E17.0"),sQuery(id+"F4.wireOp",EDGE,"E18.0"),sQuery(id+"F4.wireOp",EDGE,"E19.0"),sQuery(id+"F4.wireOp",EDGE,"E20.0"),sQuery(id+"F4.wireOp",EDGE,"E21.0"),sQuery(id+"F4.wireOp",EDGE,"E22.0"),sQuery(id+"F4.wireOp",EDGE,"E23.0"),sQuery(id+"F4.wireOp",EDGE,"E24.0")])],"isStart":false})]});
            var Q21;
            Q21=makeQuery(id+"F5.boolean.opBoolean","INTERSECT",EDGE,{"derivedFrom":[makeQuery(id+"F1.opExtrude","SWEPT_FACE",FACE,{"disambiguationData":[OSD([sQuery(id+"F0.wireOp",EDGE,"E0.sketch_text.stroke-80")])]}),makeQuery(id+"F5.opExtrude","CAP_FACE",FACE,{"disambiguationData":[OSD([sQuery(id+"F4.wireOp",EDGE,"E13.0"),sQuery(id+"F4.wireOp",EDGE,"E14.0"),sQuery(id+"F4.wireOp",EDGE,"E15.0"),sQuery(id+"F4.wireOp",EDGE,"E16.0"),sQuery(id+"F4.wireOp",EDGE,"E17.0"),sQuery(id+"F4.wireOp",EDGE,"E18.0"),sQuery(id+"F4.wireOp",EDGE,"E19.0"),sQuery(id+"F4.wireOp",EDGE,"E20.0"),sQuery(id+"F4.wireOp",EDGE,"E21.0"),sQuery(id+"F4.wireOp",EDGE,"E22.0"),sQuery(id+"F4.wireOp",EDGE,"E23.0"),sQuery(id+"F4.wireOp",EDGE,"E24.0")])],"isStart":false})]});
            var Q22;
            Q22=makeQuery(id+"F5.boolean.opBoolean","INTERSECT",EDGE,{"derivedFrom":[makeQuery(id+"F1.opExtrude","SWEPT_FACE",FACE,{"disambiguationData":[OSD([sQuery(id+"F0.wireOp",EDGE,"E0.sketch_text.stroke-71")])]}),makeQuery(id+"F5.opExtrude","CAP_FACE",FACE,{"disambiguationData":[OSD([sQuery(id+"F4.wireOp",EDGE,"E13.0"),sQuery(id+"F4.wireOp",EDGE,"E14.0"),sQuery(id+"F4.wireOp",EDGE,"E15.0"),sQuery(id+"F4.wireOp",EDGE,"E16.0"),sQuery(id+"F4.wireOp",EDGE,"E17.0"),sQuery(id+"F4.wireOp",EDGE,"E18.0"),sQuery(id+"F4.wireOp",EDGE,"E19.0"),sQuery(id+"F4.wireOp",EDGE,"E20.0"),sQuery(id+"F4.wireOp",EDGE,"E21.0"),sQuery(id+"F4.wireOp",EDGE,"E22.0"),sQuery(id+"F4.wireOp",EDGE,"E23.0"),sQuery(id+"F4.wireOp",EDGE,"E24.0")])],"isStart":false})]});
            var Q23;
            Q23=makeQuery(id+"F5.boolean.opBoolean","INTERSECT",EDGE,{"derivedFrom":[makeQuery(id+"F1.opExtrude","SWEPT_FACE",FACE,{"disambiguationData":[OSD([sQuery(id+"F0.wireOp",EDGE,"E0.sketch_text.stroke-91")])]}),makeQuery(id+"F5.opExtrude","CAP_FACE",FACE,{"disambiguationData":[OSD([sQuery(id+"F4.wireOp",EDGE,"E13.0"),sQuery(id+"F4.wireOp",EDGE,"E14.0"),sQuery(id+"F4.wireOp",EDGE,"E15.0"),sQuery(id+"F4.wireOp",EDGE,"E16.0"),sQuery(id+"F4.wireOp",EDGE,"E17.0"),sQuery(id+"F4.wireOp",EDGE,"E18.0"),sQuery(id+"F4.wireOp",EDGE,"E19.0"),sQuery(id+"F4.wireOp",EDGE,"E20.0"),sQuery(id+"F4.wireOp",EDGE,"E21.0"),sQuery(id+"F4.wireOp",EDGE,"E22.0"),sQuery(id+"F4.wireOp",EDGE,"E23.0"),sQuery(id+"F4.wireOp",EDGE,"E24.0")])],"isStart":false})]});
            var Q24;
            Q24=makeQuery(id+"F5.boolean.opBoolean","INTERSECT",EDGE,{"derivedFrom":[makeQuery(id+"F1.opExtrude","SWEPT_FACE",FACE,{"disambiguationData":[OSD([sQuery(id+"F0.wireOp",EDGE,"E0.sketch_text.stroke-90")])]}),makeQuery(id+"F5.opExtrude","CAP_FACE",FACE,{"disambiguationData":[OSD([sQuery(id+"F4.wireOp",EDGE,"E13.0"),sQuery(id+"F4.wireOp",EDGE,"E14.0"),sQuery(id+"F4.wireOp",EDGE,"E15.0"),sQuery(id+"F4.wireOp",EDGE,"E16.0"),sQuery(id+"F4.wireOp",EDGE,"E17.0"),sQuery(id+"F4.wireOp",EDGE,"E18.0"),sQuery(id+"F4.wireOp",EDGE,"E19.0"),sQuery(id+"F4.wireOp",EDGE,"E20.0"),sQuery(id+"F4.wireOp",EDGE,"E21.0"),sQuery(id+"F4.wireOp",EDGE,"E22.0"),sQuery(id+"F4.wireOp",EDGE,"E23.0"),sQuery(id+"F4.wireOp",EDGE,"E24.0")])],"isStart":false})]});
            var Q25;
            Q25=makeQuery(id+"F5.boolean.opBoolean","INTERSECT",EDGE,{"derivedFrom":[makeQuery(id+"F1.opExtrude","SWEPT_FACE",FACE,{"disambiguationData":[OSD([sQuery(id+"F0.wireOp",EDGE,"E0.sketch_text.stroke-87")])]}),makeQuery(id+"F5.opExtrude","CAP_FACE",FACE,{"disambiguationData":[OSD([sQuery(id+"F4.wireOp",EDGE,"E13.0"),sQuery(id+"F4.wireOp",EDGE,"E14.0"),sQuery(id+"F4.wireOp",EDGE,"E15.0"),sQuery(id+"F4.wireOp",EDGE,"E16.0"),sQuery(id+"F4.wireOp",EDGE,"E17.0"),sQuery(id+"F4.wireOp",EDGE,"E18.0"),sQuery(id+"F4.wireOp",EDGE,"E19.0"),sQuery(id+"F4.wireOp",EDGE,"E20.0"),sQuery(id+"F4.wireOp",EDGE,"E21.0"),sQuery(id+"F4.wireOp",EDGE,"E22.0"),sQuery(id+"F4.wireOp",EDGE,"E23.0"),sQuery(id+"F4.wireOp",EDGE,"E24.0")])],"isStart":false})]});
            var Q26;
            Q26=makeQuery(id+"F5.boolean.opBoolean","INTERSECT",EDGE,{"derivedFrom":[makeQuery(id+"F1.opExtrude","SWEPT_FACE",FACE,{"disambiguationData":[OSD([sQuery(id+"F0.wireOp",EDGE,"E0.sketch_text.stroke-85")])]}),makeQuery(id+"F5.opExtrude","CAP_FACE",FACE,{"disambiguationData":[OSD([sQuery(id+"F4.wireOp",EDGE,"E13.0"),sQuery(id+"F4.wireOp",EDGE,"E14.0"),sQuery(id+"F4.wireOp",EDGE,"E15.0"),sQuery(id+"F4.wireOp",EDGE,"E16.0"),sQuery(id+"F4.wireOp",EDGE,"E17.0"),sQuery(id+"F4.wireOp",EDGE,"E18.0"),sQuery(id+"F4.wireOp",EDGE,"E19.0"),sQuery(id+"F4.wireOp",EDGE,"E20.0"),sQuery(id+"F4.wireOp",EDGE,"E21.0"),sQuery(id+"F4.wireOp",EDGE,"E22.0"),sQuery(id+"F4.wireOp",EDGE,"E23.0"),sQuery(id+"F4.wireOp",EDGE,"E24.0")])],"isStart":false})]});
            var Q27;
            Q27=makeQuery(id+"F5.boolean.opBoolean","INTERSECT",EDGE,{"derivedFrom":[makeQuery(id+"F1.opExtrude","SWEPT_FACE",FACE,{"disambiguationData":[OSD([sQuery(id+"F0.wireOp",EDGE,"E0.sketch_text.stroke-96")])]}),makeQuery(id+"F5.opExtrude","CAP_FACE",FACE,{"disambiguationData":[OSD([sQuery(id+"F4.wireOp",EDGE,"E13.0"),sQuery(id+"F4.wireOp",EDGE,"E14.0"),sQuery(id+"F4.wireOp",EDGE,"E15.0"),sQuery(id+"F4.wireOp",EDGE,"E16.0"),sQuery(id+"F4.wireOp",EDGE,"E17.0"),sQuery(id+"F4.wireOp",EDGE,"E18.0"),sQuery(id+"F4.wireOp",EDGE,"E19.0"),sQuery(id+"F4.wireOp",EDGE,"E20.0"),sQuery(id+"F4.wireOp",EDGE,"E21.0"),sQuery(id+"F4.wireOp",EDGE,"E22.0"),sQuery(id+"F4.wireOp",EDGE,"E23.0"),sQuery(id+"F4.wireOp",EDGE,"E24.0")])],"isStart":false})]});
            var Q28;
            Q28=makeQuery(id+"F5.boolean.opBoolean","INTERSECT",EDGE,{"derivedFrom":[makeQuery(id+"F1.opExtrude","SWEPT_FACE",FACE,{"disambiguationData":[OSD([sQuery(id+"F0.wireOp",EDGE,"E0.sketch_text.stroke-92")])]}),makeQuery(id+"F5.opExtrude","CAP_FACE",FACE,{"disambiguationData":[OSD([sQuery(id+"F4.wireOp",EDGE,"E13.0"),sQuery(id+"F4.wireOp",EDGE,"E14.0"),sQuery(id+"F4.wireOp",EDGE,"E15.0"),sQuery(id+"F4.wireOp",EDGE,"E16.0"),sQuery(id+"F4.wireOp",EDGE,"E17.0"),sQuery(id+"F4.wireOp",EDGE,"E18.0"),sQuery(id+"F4.wireOp",EDGE,"E19.0"),sQuery(id+"F4.wireOp",EDGE,"E20.0"),sQuery(id+"F4.wireOp",EDGE,"E21.0"),sQuery(id+"F4.wireOp",EDGE,"E22.0"),sQuery(id+"F4.wireOp",EDGE,"E23.0"),sQuery(id+"F4.wireOp",EDGE,"E24.0")])],"isStart":false})]});
            var Q29;
            Q29=makeQuery(id+"F5.boolean.opBoolean","INTERSECT",EDGE,{"derivedFrom":[makeQuery(id+"F1.opExtrude","SWEPT_FACE",FACE,{"disambiguationData":[OSD([sQuery(id+"F0.wireOp",EDGE,"E0.sketch_text.stroke-93")])]}),makeQuery(id+"F5.opExtrude","CAP_FACE",FACE,{"disambiguationData":[OSD([sQuery(id+"F4.wireOp",EDGE,"E13.0"),sQuery(id+"F4.wireOp",EDGE,"E14.0"),sQuery(id+"F4.wireOp",EDGE,"E15.0"),sQuery(id+"F4.wireOp",EDGE,"E16.0"),sQuery(id+"F4.wireOp",EDGE,"E17.0"),sQuery(id+"F4.wireOp",EDGE,"E18.0"),sQuery(id+"F4.wireOp",EDGE,"E19.0"),sQuery(id+"F4.wireOp",EDGE,"E20.0"),sQuery(id+"F4.wireOp",EDGE,"E21.0"),sQuery(id+"F4.wireOp",EDGE,"E22.0"),sQuery(id+"F4.wireOp",EDGE,"E23.0"),sQuery(id+"F4.wireOp",EDGE,"E24.0")])],"isStart":false})]});
            fillet(context, id + "F8", {"entities" : qUnion([Q0, Q1, Q2, Q3, Q4, Q5, Q6, Q7, Q8, Q9, Q10, Q11, Q12, Q13, Q14, Q15, Q16, Q17, Q18, Q19, Q20, Q21, Q22, Q23, Q24, Q25, Q26, Q27, Q28, Q29]), "radius" : 0.8 * mm, "tangentPropagation" : true, "allowEdgeOverflow" : false});
        }
        {
            var Q0;
            Q0=makeQuery(id+"F5.boolean.opBoolean","SPLIT",FACE,{"disambiguationData":[TD([makeQuery(id+"F1.opExtrude","SWEPT_FACE",FACE,{"disambiguationData":[OSD([sQuery(id+"F0.wireOp",EDGE,"E0.sketch_text.stroke-0")])]})])],"derivedFrom":makeQuery(id+"F5.opExtrude","CAP_FACE",FACE,{"disambiguationData":[OSD([sQuery(id+"F4.wireOp",EDGE,"E13.0"),sQuery(id+"F4.wireOp",EDGE,"E14.0"),sQuery(id+"F4.wireOp",EDGE,"E15.0"),sQuery(id+"F4.wireOp",EDGE,"E16.0"),sQuery(id+"F4.wireOp",EDGE,"E17.0"),sQuery(id+"F4.wireOp",EDGE,"E18.0"),sQuery(id+"F4.wireOp",EDGE,"E19.0"),sQuery(id+"F4.wireOp",EDGE,"E20.0"),sQuery(id+"F4.wireOp",EDGE,"E21.0"),sQuery(id+"F4.wireOp",EDGE,"E22.0"),sQuery(id+"F4.wireOp",EDGE,"E23.0"),sQuery(id+"F4.wireOp",EDGE,"E24.0")])],"isStart":false})});
            var sketch = newSketch(context, id + "F9", { "sketchPlane" : qUnion([Q0])});
            skCircle(sketch, "E29", {"center": v(-6.35, -19.05) * mm, "radius": 6.35 * mm});
            skCircle(sketch, "E30", {"center": v(-6.35, 6.35) * mm, "radius": 6.35 * mm});
            skCircle(sketch, "E31", {"center": v(57.15, -19.05) * mm, "radius": 6.35 * mm});
            skCircle(sketch, "E32", {"center": v(57.15, 6.35) * mm, "radius": 6.35 * mm});
            skSolve(sketch);
        }
        {
            var Q0;
            Q0 = qSketchRegion(id + "F9", true);
            extrude(context, id + "F10", {"entities" : qUnion([Q0]), "operationType" : NewBodyOperationType.REMOVE, "endBound" : BoundingType.THROUGH_ALL, "oppositeDirection" : true, "depth" : 25.4 * mm});
        }
        {
            var Q0;
            Q0=makeQuery(id+"F3.opExtrude","CAP_EDGE",EDGE,{"disambiguationData":[OSD([sQuery(id+"F2.wireOp",EDGE,"E12.3")])],"isStart":false});
            chamfer(context, id + "F11", {"entities" : qUnion([Q0]), "chamferType" : ChamferType.TWO_OFFSETS, "width1" : 6.35 * mm, "oppositeDirection" : false, "width2" : 0.8 * mm, "tangentPropagation" : true});
        }
        {
            var Q0;
            Q0=makeQuery(id+"F3.opExtrude","CAP_EDGE",EDGE,{"disambiguationData":[OSD([sQuery(id+"F2.wireOp",EDGE,"E5")])],"isStart":false});
            chamfer(context, id + "F12", {"entities" : qUnion([Q0]), "chamferType" : ChamferType.TWO_OFFSETS, "width1" : 1.59 * mm, "oppositeDirection" : false, "width2" : 9.52 * mm, "tangentPropagation" : true});
        }
    });
